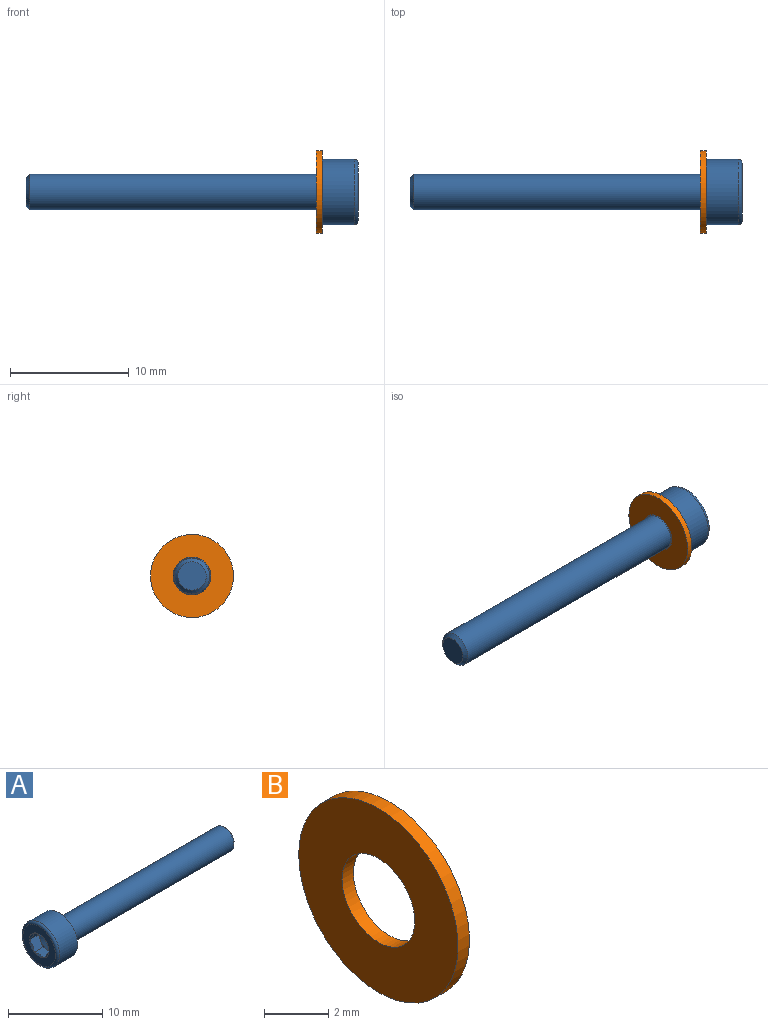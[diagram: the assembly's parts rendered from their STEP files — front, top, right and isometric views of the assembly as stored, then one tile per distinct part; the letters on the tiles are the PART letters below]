
ASSEMBLY  parts=2 mates=1
PART A: 24 faces, bbox 28x6x6 mm
  f0: plane 1.08x0.63mm, normal (-1,0,0), area 0.1mm2, adj f16,f17,f23
  f1: plane 1.25x0.36mm, normal (-1,0,0), area 0.1mm2, adj f17,f18,f23
  f2: plane 1.08x0.63mm, normal (-1,0,0), area 0.1mm2, adj f18,f19,f23
  f3: plane 1.08x0.63mm, normal (-1,0,0), area 0.1mm2, adj f19,f20,f23
  f4: plane 1.25x0.36mm, normal (-1,0,0), area 0.1mm2, adj f20,f21,f23
  f5: cone r=1.45mm half-angle=60deg, axis (-1,0,0), area 1.4mm2, adj f15,f16,f17,f18,f19,f20,f21
  f6: cone r=1.51mm half-angle=26deg, axis (-1,0,0), area 4.6mm2, adj f7,f11
  f7: torus R=1.6mm, axis (1,0,0), area 0.4mm2, adj f6,f10
  f8: plane 2.39x2.39mm, normal (1,0,0), area 4.5mm2, adj f9
  f9: cone r=1.5mm half-angle=45deg, axis (-1,0,0), area 3.7mm2, adj f8,f10
  f10: cylinder r=1.5mm len=24.18mm, axis (1,0,0), area 227.9mm2, adj f7,f9
  f11: torus R=1.8mm, axis (1,0,0), area 1.2mm2, adj f6,f13
  f12: cylinder r=2.75mm len=5.5mm, axis (1,0,0), area 46.7mm2, adj f13,f14
  f13: plane 5.5x5.5mm, normal (1,0,0), area 13.6mm2, adj f11,f12
  f14: torus R=2.45mm, axis (1,0,0), area 7.8mm2, adj f12,f15
  f15: plane 4.9x4.9mm, normal (-1,0,0), area 12.2mm2, adj f5,f14
  f16: plane 1.45x1.3mm, normal (0,0,-1), area 1.8mm2, adj f0,f5,f17,f21,f22
  f17: plane 1.29x1.25mm, normal (0,0.87,-0.5), area 1.8mm2, adj f0,f1,f5,f16,f18
  f18: plane 1.29x1.25mm, normal (0,0.87,0.5), area 1.8mm2, adj f1,f2,f5,f17,f19
  f19: plane 1.45x1.3mm, normal (0,0,1), area 1.8mm2, adj f2,f3,f5,f18,f20
  f20: plane 1.29x1.25mm, normal (0,-0.87,0.5), area 1.8mm2, adj f3,f4,f5,f19,f21
  f21: plane 1.29x1.25mm, normal (0,-0.87,-0.5), area 1.8mm2, adj f4,f5,f16,f20,f22
  f22: plane 1.08x0.63mm, normal (-1,0,0), area 0.1mm2, adj f16,f21,f23
  f23: cone r=1.25mm half-angle=60deg, axis (-1,0,0), area 5.7mm2, adj f0,f1,f2,f3,f4,f22
PART B: 4 faces, bbox 0.5x7x7 mm
  f0: plane 7x7mm, normal (-1,0,0), area 30.4mm2, adj f1,f3
  f1: cylinder r=1.6mm len=3.2mm, axis (1,0,0), area 5mm2, adj f0,f2
  f2: plane 7x7mm, normal (1,0,0), area 30.4mm2, adj f1,f3
  f3: cylinder r=3.5mm len=7mm, axis (1,0,0), area 11mm2, adj f0,f2
PLACE A rot(axis=(0,1,0),180deg) t=(0.5,0,0)mm
PLACE B at identity fixed
MATE fastened A.f5 <-> B.f1  axis (1,0,0) through (0.5,0,0)mm
